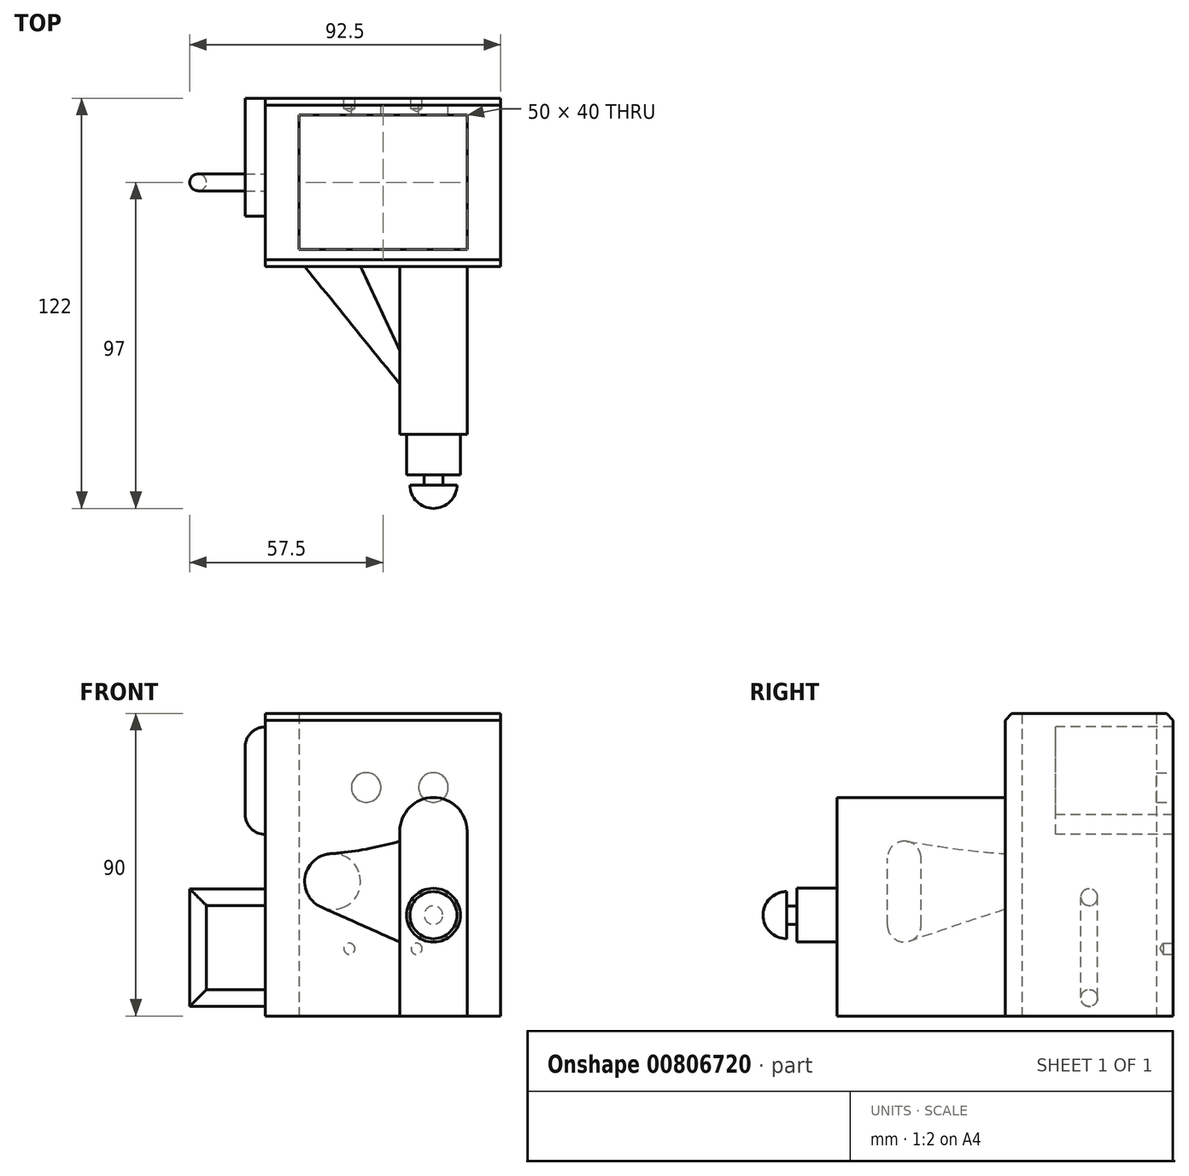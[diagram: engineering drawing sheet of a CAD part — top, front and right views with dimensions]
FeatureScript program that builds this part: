
annotation { "Feature Type Name" : "Feature", "Feature Type Description" : "" }
export const myFeature = defineFeature(function(context is Context, id is Id, definition is map)
    precondition{}
    {
        {
            var Q0;
            Q0=qCreatedBy(makeId("Top.planeOp"),FACE);
            var sketch = newSketch(context, id + "F0", { "sketchPlane" : qUnion([Q0])});
            skLineSegment(sketch, "E0.bottom", {"start": v(0, 0) * mm, "end": v(70, 0) * mm});
            skLineSegment(sketch, "E0.top", {"start": v(0, 50) * mm, "end": v(70, 50) * mm});
            skLineSegment(sketch, "E0.left", {"start": v(0, 0) * mm, "end": v(0, 50) * mm});
            skLineSegment(sketch, "E0.right", {"start": v(70, 0) * mm, "end": v(70, 50) * mm});
            skLineSegment(sketch, "E1.bottom", {"start": v(60, 5) * mm, "end": v(10, 5) * mm});
            skLineSegment(sketch, "E1.top", {"start": v(60, 45) * mm, "end": v(10, 45) * mm});
            skLineSegment(sketch, "E1.left", {"start": v(60, 5) * mm, "end": v(60, 45) * mm});
            skLineSegment(sketch, "E1.right", {"start": v(10, 5) * mm, "end": v(10, 45) * mm});
            skPoint(sketch, "E1.middle", {"position": v(35, 25) * mm});
            skLineSegment(sketch, "E2", {"start": v(35, 25) * mm, "end": v(35, 50) * mm});
            skLineSegment(sketch, "E3", {"start": v(35, 25) * mm, "end": v(0, 25) * mm});
            skSolve(sketch);
        }
        {
            var Q0;
            Q0 = qSketchRegion(id + "F0", true);
            extrude(context, id + "F1", {"entities" : qUnion([Q0]), "depth" : 90 * mm, "offsetDistance" : 25 * mm});
        }
        {
            var Q0;
            Q0=makeQuery(id+"F1.opExtrude","CAP_EDGE",EDGE,{"disambiguationData":[OSD([sQuery(id+"F0.wireOp",EDGE,"E0.bottom")])],"isStart":false});
            var Q1;
            Q1=makeQuery(id+"F1.opExtrude","CAP_EDGE",EDGE,{"disambiguationData":[OSD([sQuery(id+"F0.wireOp",EDGE,"E0.top")])],"isStart":false});
            chamfer(context, id + "F2", {"entities" : qUnion([Q0, Q1]), "width" : 2 * mm, "tangentPropagation" : true});
        }
        {
            var Q0;
            Q0=makeQuery(id+"F1.opExtrude","CAP_FACE",FACE,{"disambiguationData":[OSD([sQuery(id+"F0.wireOp",EDGE,"E0.bottom"),sQuery(id+"F0.wireOp",EDGE,"E0.top"),sQuery(id+"F0.wireOp",EDGE,"E0.left"),sQuery(id+"F0.wireOp",EDGE,"E0.right"),sQuery(id+"F0.wireOp",EDGE,"E1.bottom"),sQuery(id+"F0.wireOp",EDGE,"E1.top"),sQuery(id+"F0.wireOp",EDGE,"E1.left"),sQuery(id+"F0.wireOp",EDGE,"E1.right")])],"isStart":false});
            var sketch = newSketch(context, id + "F3", { "sketchPlane" : qUnion([Q0])});
            skLineSegment(sketch, "E4", {"start": v(0, 25) * mm, "end": v(70, 25) * mm});
            skSolve(sketch);
        }
        {
            var Q0;
            Q0=makeQuery(id+"F1.opExtrude","SWEPT_FACE",FACE,{"disambiguationData":[OSD([sQuery(id+"F0.wireOp",EDGE,"E0.bottom")])]});
            var Q1;
            Q1=sQuery(id+"F3.wireOp",EDGE,"E4");
            cPlane(context, id + "F4", {"entities" : qUnion([Q0, Q1]), "cplaneType" : CPlaneType.LINE_ANGLE, "offset" : 25 * mm, "angle" : 0 * degree, "width" : 150 * mm, "height" : 150 * mm});
        }
        {
            var Q0;
            Q0=makeQuery(id+"F1.opExtrude","SWEPT_FACE",FACE,{"disambiguationData":[OSD([sQuery(id+"F0.wireOp",EDGE,"E0.left")])]});
            var sketch = newSketch(context, id + "F5", { "sketchPlane" : qUnion([Q0])});
            skLineSegment(sketch, "E5", {"start": v(-25, 0) * mm, "end": v(-25, 90) * mm});
            skSolve(sketch);
        }
        {
            var Q0;
            Q0=qCreatedBy(id+"F4.planeOp",FACE);
            var sketch = newSketch(context, id + "F6", { "sketchPlane" : qUnion([Q0])});
            skArc(sketch, "E6", {"start": v(6, 80) * mm, "mid": v(4.24, 84.24) * mm, "end": v(0, 86) * mm});
            skArc(sketch, "E7", {"start": v(0, 54) * mm, "mid": v(4.27, 55.78) * mm, "end": v(6, 60.07) * mm});
            skLineSegment(sketch, "E8", {"start": v(6, 59.93) * mm, "end": v(6, 80) * mm});
            skLineSegment(sketch, "E9", {"start": v(0, 54) * mm, "end": v(0, 86) * mm});
            skSolve(sketch);
        }
        {
            var Q0;
            {var subQ1=sQuery(id+"F6.wireOp",EDGE,"E6");Q0=makeQuery(id+"F6.imprint","IMPRINT",FACE,{"disambiguationData":[TD([[makeQuery(id+"F6.imprint","IMPRINT",EDGE,{"derivedFrom":subQ1}),1.0]])]});}
            extrude(context, id + "F7", {"entities" : qUnion([Q0]), "operationType" : NewBodyOperationType.ADD, "depth" : 25 * mm, "offsetDistance" : 25 * mm, "hasSecondDirection" : true, "secondDirectionOppositeDirection" : true, "secondDirectionDepth" : 10 * mm});
        }
        {
            var Q0;
            Q0=qCreatedBy(id+"F4.planeOp",FACE);
            var sketch = newSketch(context, id + "F8", { "sketchPlane" : qUnion([Q0])});
            skLineSegment(sketch, "E10", {"start": v(0, 35.36) * mm, "end": v(20, 35.36) * mm});
            skLineSegment(sketch, "E11", {"start": v(20, 35.36) * mm, "end": v(20, 5.36) * mm});
            skLineSegment(sketch, "E12", {"start": v(20, 5.36) * mm, "end": v(0, 5.36) * mm});
            skSolve(sketch);
        }
        {
            var Q0;
            Q0=qCreatedBy(makeId("Right.planeOp"),FACE);
            var sketch = newSketch(context, id + "F9", { "sketchPlane" : qUnion([Q0])});
            skCircle(sketch, "E13", {"center": v(25, 5.36) * mm, "radius": 2.5 * mm});
            skSolve(sketch);
        }
        {
            var Q0;
            Q0 = qSketchRegion(id + "F9", true);
            var Q1;
            Q1 = qConstructionFilter(qBodyType(qCreatedBy(id + "F8" ,EDGE), BodyType.WIRE), ConstructionObject.NO);
            sweep(context, id + "F10", {"operationType" : NewBodyOperationType.ADD, "profiles" : qUnion([Q0]), "path" : qUnion([Q1])});
        }
        {
            var Q0;
            Q0=makeQuery(id+"F1.opExtrude","SWEPT_FACE",FACE,{"disambiguationData":[OSD([sQuery(id+"F0.wireOp",EDGE,"E0.bottom")])]});
            var sketch = newSketch(context, id + "F11", { "sketchPlane" : qUnion([Q0])});
            skSolve(sketch);
        }
        {
            var Q0;
            {var subQ0=sQuery(id+"F0.wireOp",EDGE,"E0.bottom");Q0=makeQuery(id+"F11.imprint","IMPRINT",FACE,{"disambiguationData":[TD([[makeQuery(id+"F11.imprint","IMPRINT",EDGE,{"derivedFrom":makeQuery(id+"F1.opExtrude","CAP_EDGE",EDGE,{"disambiguationData":[OSD([subQ0])],"isStart":true})}),1.0]])]});}
            var sketch = newSketch(context, id + "F12", { "sketchPlane" : qUnion([Q0])});
            skArc(sketch, "E14", {"start": v(60, 55) * mm, "mid": v(50, 65) * mm, "end": v(40, 55) * mm});
            skLineSegment(sketch, "E15", {"start": v(40, 55) * mm, "end": v(40, 0) * mm});
            skLineSegment(sketch, "E16", {"start": v(40, 0) * mm, "end": v(60, 0) * mm});
            skLineSegment(sketch, "E17", {"start": v(60, 0) * mm, "end": v(60, 55) * mm});
            skSolve(sketch);
        }
        {
            var Q0;
            Q0=makeQuery(id+"F12.imprint","IMPRINT",FACE,{"disambiguationData":[TD([[makeQuery(id+"F12.imprint","IMPRINT",EDGE,{"derivedFrom":sQuery(id+"F12.wireOp",EDGE,"E14")}),1.0]])]});
            extrude(context, id + "F13", {"entities" : qUnion([Q0]), "operationType" : NewBodyOperationType.ADD, "depth" : 50 * mm, "offsetDistance" : 25 * mm});
        }
        {
            var Q0;
            Q0=qCreatedBy(makeId("Right.planeOp"),FACE);
            cPlane(context, id + "F14", {"entities" : qUnion([Q0]), "cplaneType" : CPlaneType.OFFSET, "offset" : 50 * mm, "width" : 150 * mm, "height" : 150 * mm});
        }
        {
            var Q0;
            Q0=makeQuery(id+"F13.opExtrude","CAP_FACE",FACE,{"disambiguationData":[OSD([sQuery(id+"F12.wireOp",EDGE,"E14"),sQuery(id+"F12.wireOp",EDGE,"E15"),sQuery(id+"F12.wireOp",EDGE,"E16"),sQuery(id+"F12.wireOp",EDGE,"E17")])],"isStart":false});
            var sketch = newSketch(context, id + "F15", { "sketchPlane" : qUnion([Q0])});
            skLineSegment(sketch, "E18", {"start": v(50, 0) * mm, "end": v(50, 65) * mm, "construction": true});
            skSolve(sketch);
        }
        {
            var Q0;
            Q0=qCreatedBy(id+"F14.planeOp",FACE);
            var sketch = newSketch(context, id + "F16", { "sketchPlane" : qUnion([Q0])});
            skLineSegment(sketch, "E19.bottom", {"start": v(-50, 30) * mm, "end": v(-62, 30) * mm});
            skLineSegment(sketch, "E19.top", {"start": v(-50, 38) * mm, "end": v(-62, 38) * mm});
            skLineSegment(sketch, "E19.left", {"start": v(-50, 30) * mm, "end": v(-50, 38) * mm});
            skLineSegment(sketch, "E20", {"start": v(-50, 34) * mm, "end": v(-62, 34) * mm, "construction": true});
            skPoint(sketch, "E21.middle", {"position": v(-62, 34) * mm});
            skPoint(sketch, "E22.orphan", {"position": v(-59, 31) * mm});
            skPoint(sketch, "E23.orphan", {"position": v(-59, 37) * mm});
            skLineSegment(sketch, "E24", {"start": v(-62, 30) * mm, "end": v(-65, 30) * mm});
            skLineSegment(sketch, "E25.trimOffspring", {"start": v(-61.96, 37) * mm, "end": v(-62, 38) * mm});
            skArc(sketch, "E26", {"start": v(-65, 37) * mm, "mid": v(-69.95, 34.95) * mm, "end": v(-72, 30) * mm});
            skLineSegment(sketch, "E27", {"start": v(-65, 30) * mm, "end": v(-72, 30) * mm});
            skPoint(sketch, "E28.end.orphan", {"position": v(-65, 31) * mm});
            skPoint(sketch, "E29.end.orphan", {"position": v(-65, 40.51) * mm});
            skLineSegment(sketch, "E30", {"start": v(-65, 37) * mm, "end": v(-65, 32.75) * mm});
            skLineSegment(sketch, "E31", {"start": v(-61.96, 37) * mm, "end": v(-61.96, 32.75) * mm});
            skLineSegment(sketch, "E32", {"start": v(-61.96, 32.75) * mm, "end": v(-65, 32.75) * mm});
            skSolve(sketch);
        }
        {
            var Q0;
            Q0=makeQuery(id+"F16.imprint","IMPRINT",FACE,{"disambiguationData":[TD([[makeQuery(id+"F16.imprint","IMPRINT",EDGE,{"derivedFrom":sQuery(id+"F16.wireOp",EDGE,"E19.bottom")}),-1.0]])]});
            var Q1;
            Q1=sQuery(id+"F16.wireOp",EDGE,"E19.bottom");
            revolve(context, id + "F17", {"operationType" : NewBodyOperationType.ADD, "surfaceOperationType" : NewSurfaceOperationType.NEW, "entities" : qUnion([Q0]), "axis" : qUnion([Q1]), "revolveType" : RevolveType.FULL});
        }
        {
            var Q0;
            {var subQ0=sQuery(id+"F0.wireOp",EDGE,"E0.bottom");Q0=makeQuery(id+"F11.imprint","IMPRINT",FACE,{"disambiguationData":[TD([[makeQuery(id+"F11.imprint","IMPRINT",EDGE,{"derivedFrom":makeQuery(id+"F1.opExtrude","CAP_EDGE",EDGE,{"disambiguationData":[OSD([subQ0])],"isStart":true})}),1.0]])]});}
            var sketch = newSketch(context, id + "F18", { "sketchPlane" : qUnion([Q0])});
            skCircle(sketch, "E33", {"center": v(20, 40) * mm, "radius": 8.3 * mm});
            skSolve(sketch);
        }
        {
            var Q0;
            Q0=makeQuery(id+"F13.opExtrude","SWEPT_FACE",FACE,{"disambiguationData":[OSD([sQuery(id+"F12.wireOp",EDGE,"E15")])]});
            var sketch = newSketch(context, id + "F19", { "sketchPlane" : qUnion([Q0])});
            skLineSegment(sketch, "E34", {"start": v(30, -33.02) * mm, "end": v(30, 87.7) * mm, "construction": true});
            skArc(sketch, "E35", {"start": v(35, 47) * mm, "mid": v(30, 52) * mm, "end": v(25, 47) * mm});
            skArc(sketch, "E36", {"start": v(25, 27) * mm, "mid": v(30, 22) * mm, "end": v(35, 27) * mm});
            skLineSegment(sketch, "E37", {"start": v(25, 27) * mm, "end": v(25, 47) * mm});
            skLineSegment(sketch, "E38", {"start": v(35, 27) * mm, "end": v(35, 47) * mm});
            skSolve(sketch);
        }
        {
            var Q1;
            Q1 = qSketchRegion(id + "F18", true);
            var Q2;
            Q2 = qSketchRegion(id + "F19", true);
            loft(context, id + "F20", {"operationType" : NewBodyOperationType.ADD, "sheetProfilesArray" : [{ "sheetProfileEntities" : qUnion([Q1]) }, { "sheetProfileEntities" : qUnion([Q2]) }]});
        }
        {
            var Q0;
            Q0=makeQuery(id+"F7.boolean.opBoolean","MERGE",FACE,{"derivedFrom":[makeQuery(id+"F1.opExtrude","SWEPT_FACE",FACE,{"disambiguationData":[OSD([sQuery(id+"F0.wireOp",EDGE,"E0.top")])]}),makeQuery(id+"F7.opExtrude","CAP_FACE",FACE,{"disambiguationData":[OSD([sQuery(id+"F6.wireOp",EDGE,"E6"),sQuery(id+"F6.wireOp",EDGE,"E7"),sQuery(id+"F6.wireOp",EDGE,"E8"),sQuery(id+"F6.wireOp",EDGE,"E9")])],"isStart":false})]});
            var sketch = newSketch(context, id + "F21", { "sketchPlane" : qUnion([Q0])});
            skLineSegment(sketch, "E39", {"start": v(-62.97, 68) * mm, "end": v(-10, 68) * mm, "construction": true});
            skPoint(sketch, "E40", {"position": v(-50, 68) * mm});
            skPoint(sketch, "E41", {"position": v(-30, 68) * mm});
            skSolve(sketch);
        }
        {
            var Q0;
            Q0=sQuery(id+"F21.wireOp",VERTEX,"E40");
            var Q1;
            Q1=sQuery(id+"F21.wireOp",VERTEX,"E41");
            var Q2;
            Q2=makeQuery(id+"F1.opExtrude","SWEPT_BODY",BODY,{"disambiguationData":[OSD([sQuery(id+"F0.wireOp",EDGE,"E0.bottom"),sQuery(id+"F0.wireOp",EDGE,"E0.top"),sQuery(id+"F0.wireOp",EDGE,"E0.left"),sQuery(id+"F0.wireOp",EDGE,"E0.right"),sQuery(id+"F0.wireOp",EDGE,"E1.bottom"),sQuery(id+"F0.wireOp",EDGE,"E1.top"),sQuery(id+"F0.wireOp",EDGE,"E1.left"),sQuery(id+"F0.wireOp",EDGE,"E1.right")])]});
            hole(context, id + "F22", {"style" : HoleStyle.SIMPLE, "endStyle" : HoleEndStyle.BLIND, "standardTappedOrClearance" : lookupTablePath({ "standard" : "ISO", "fit" : "Normal", "size" : "M8", "type" : "Clearance" }), "standardBlindInLast" : lookupTablePath({ "fit" : "Standard", "standard" : "ISO", "size" : "M8", "type" : "Clearance" }), "holeDiameter" : 8.8 * mm, "majorDiameter" : 8 * mm, "holeDepth" : 15.75 * mm, "isTappedThrough" : true, "tappedDepth" : 12 * mm, "tapClearance" : 3, "locations" : qUnion([Q0, Q1]), "scope" : qUnion([Q2])});
        }
        {
            var Q0;
            Q0=makeQuery(id+"F7.boolean.opBoolean","MERGE",FACE,{"derivedFrom":[makeQuery(id+"F1.opExtrude","SWEPT_FACE",FACE,{"disambiguationData":[OSD([sQuery(id+"F0.wireOp",EDGE,"E0.top")])]}),makeQuery(id+"F7.opExtrude","CAP_FACE",FACE,{"disambiguationData":[OSD([sQuery(id+"F6.wireOp",EDGE,"E6"),sQuery(id+"F6.wireOp",EDGE,"E7"),sQuery(id+"F6.wireOp",EDGE,"E8"),sQuery(id+"F6.wireOp",EDGE,"E9")])],"isStart":false})]});
            var sketch = newSketch(context, id + "F23", { "sketchPlane" : qUnion([Q0])});
            skLineSegment(sketch, "E42", {"start": v(-49.87, 20) * mm, "end": v(-17.6, 20) * mm, "construction": true});
            skPoint(sketch, "E43", {"position": v(-45, 20) * mm});
            skPoint(sketch, "E44", {"position": v(-25, 20) * mm});
            skSolve(sketch);
        }
        {
            var Q0;
            Q0=sQuery(id+"F23.wireOp",VERTEX,"E43");
            var Q1;
            Q1=sQuery(id+"F23.wireOp",VERTEX,"E44");
            var Q2;
            Q2=makeQuery(id+"F1.opExtrude","SWEPT_BODY",BODY,{"disambiguationData":[OSD([sQuery(id+"F0.wireOp",EDGE,"E0.bottom"),sQuery(id+"F0.wireOp",EDGE,"E0.top"),sQuery(id+"F0.wireOp",EDGE,"E0.left"),sQuery(id+"F0.wireOp",EDGE,"E0.right"),sQuery(id+"F0.wireOp",EDGE,"E1.bottom"),sQuery(id+"F0.wireOp",EDGE,"E1.top"),sQuery(id+"F0.wireOp",EDGE,"E1.left"),sQuery(id+"F0.wireOp",EDGE,"E1.right")])]});
            hole(context, id + "F24", {"style" : HoleStyle.SIMPLE, "endStyle" : HoleEndStyle.BLIND, "standardTappedOrClearance" : lookupTablePath({ "standard" : "ISO", "fit" : "Normal", "size" : "M3", "type" : "Clearance" }), "standardBlindInLast" : lookupTablePath({ "fit" : "Standard", "standard" : "ISO", "size" : "M3", "type" : "Clearance" }), "holeDiameter" : 3.3 * mm, "majorDiameter" : 5 * mm, "holeDepth" : 3 * mm, "isTappedThrough" : true, "tappedDepth" : 12 * mm, "tapClearance" : 3, "locations" : qUnion([Q0, Q1]), "scope" : qUnion([Q2])});
        }
    });
